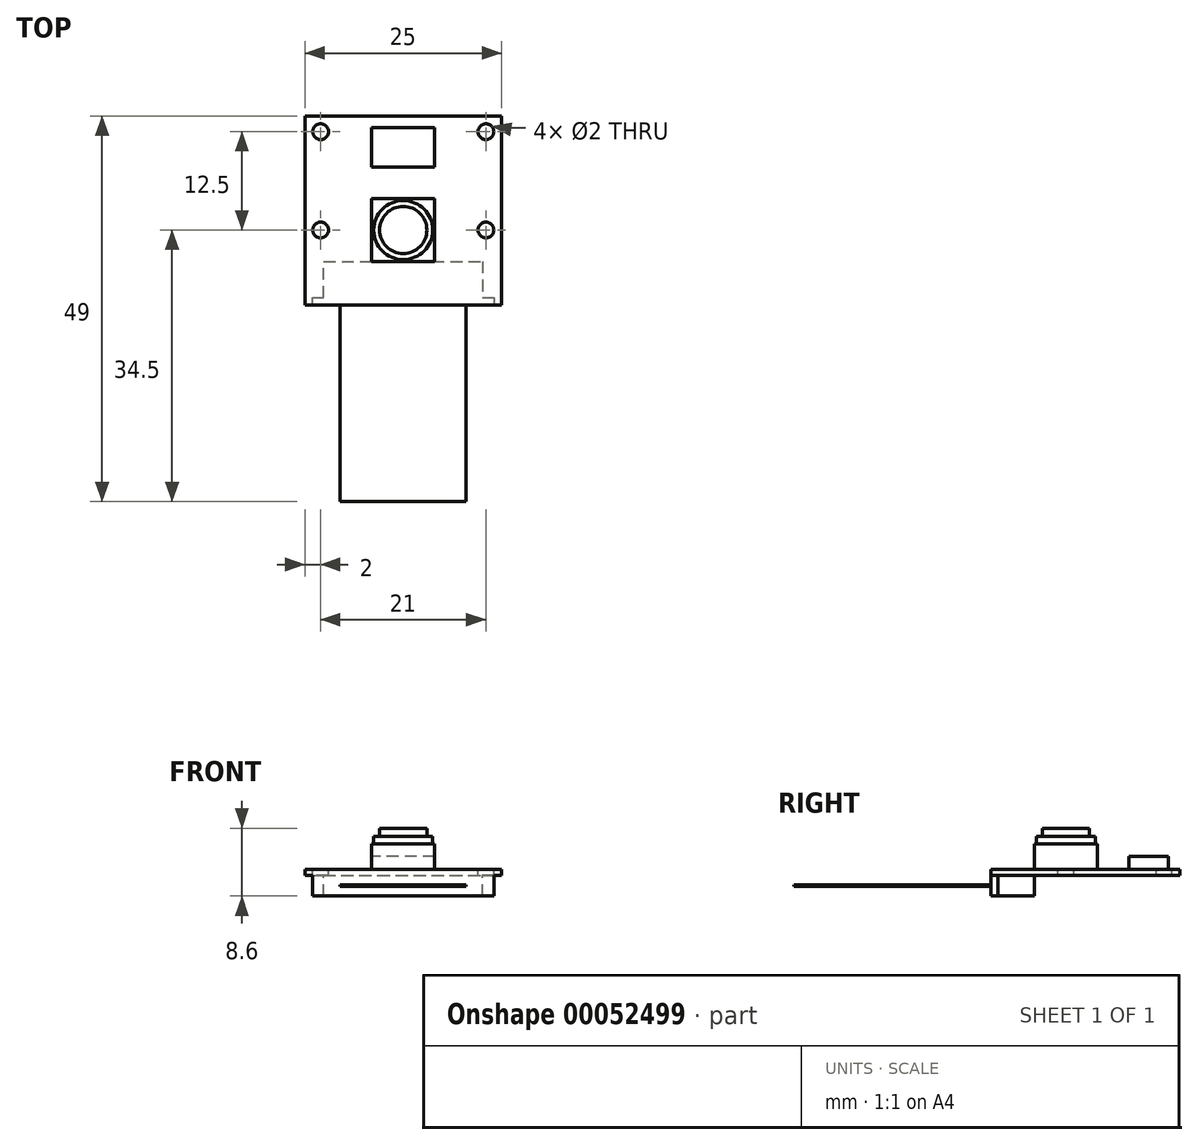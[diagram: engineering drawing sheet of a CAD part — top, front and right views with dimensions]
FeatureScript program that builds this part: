
annotation { "Feature Type Name" : "Feature", "Feature Type Description" : "" }
export const myFeature = defineFeature(function(context is Context, id is Id, definition is map)
    precondition{}
    {
        {
            var Q0;
            Q0=qCreatedBy(makeId("Top.planeOp"),FACE);
            var sketch = newSketch(context, id + "F0", { "sketchPlane" : qUnion([Q0])});
            skLineSegment(sketch, "E0.bottom", {"start": v(-12.5, 14.5) * mm, "end": v(12.5, 14.5) * mm});
            skLineSegment(sketch, "E0.top", {"start": v(-12.5, -9.5) * mm, "end": v(12.5, -9.5) * mm});
            skLineSegment(sketch, "E0.left", {"start": v(-12.5, 14.5) * mm, "end": v(-12.5, -9.5) * mm});
            skLineSegment(sketch, "E0.right", {"start": v(12.5, 14.5) * mm, "end": v(12.5, -9.5) * mm});
            skSolve(sketch);
        }
        {
            var Q0;
            Q0 = qSketchRegion(id + "F0", true);
            extrude(context, id + "F1", {"entities" : qUnion([Q0]), "oppositeDirection" : true, "depth" : .8 * mm});
        }
        {
            var Q0;
            Q0=makeQuery(id+"F1.opExtrude","CAP_FACE",FACE,{"disambiguationData":[OSD([sQuery(id+"F0.wireOp",EDGE,"E0.bottom"),sQuery(id+"F0.wireOp",EDGE,"E0.top"),sQuery(id+"F0.wireOp",EDGE,"E0.left"),sQuery(id+"F0.wireOp",EDGE,"E0.right")])],"isStart":true});
            var sketch = newSketch(context, id + "F2", { "sketchPlane" : qUnion([Q0])});
            skLineSegment(sketch, "E1.rect.bottom", {"start": v(4, 4) * mm, "end": v(-4, 4) * mm});
            skLineSegment(sketch, "E1.rect.top", {"start": v(4, -4) * mm, "end": v(-4, -4) * mm});
            skLineSegment(sketch, "E1.rect.left", {"start": v(4, 4) * mm, "end": v(4, -4) * mm});
            skLineSegment(sketch, "E1.rect.right", {"start": v(-4, 4) * mm, "end": v(-4, -4) * mm});
            skPoint(sketch, "E1.rect.middle", {"position": v(0, 0) * mm});
            skSolve(sketch);
        }
        {
            var Q0;
            Q0 = qSketchRegion(id + "F2", true);
            extrude(context, id + "F3", {"entities" : qUnion([Q0]), "operationType" : NewBodyOperationType.ADD, "depth" : 3.2 * mm});
        }
        {
            var Q0;
            Q0=makeQuery(id+"F3.opExtrude","CAP_FACE",FACE,{"disambiguationData":[OSD([sQuery(id+"F2.wireOp",EDGE,"E1.rect.bottom"),sQuery(id+"F2.wireOp",EDGE,"E1.rect.top"),sQuery(id+"F2.wireOp",EDGE,"E1.rect.left"),sQuery(id+"F2.wireOp",EDGE,"E1.rect.right")])],"isStart":false});
            var sketch = newSketch(context, id + "F4", { "sketchPlane" : qUnion([Q0])});
            skCircle(sketch, "E2", {"center": v(0, 0) * mm, "radius": 3.75 * mm});
            skSolve(sketch);
        }
        {
            var Q0;
            Q0 = qSketchRegion(id + "F4", true);
            var Q1;
            Q1=sQuery(id+"F4.wireOp",EDGE,"E2");
            extrude(context, id + "F5", {"entities" : qUnion([Q0]), "operationType" : NewBodyOperationType.ADD, "surfaceEntities" : qUnion([Q1]), "depth" : 1 * mm});
        }
        {
            var Q0;
            Q0=makeQuery(id+"F5.opExtrude","CAP_FACE",FACE,{"disambiguationData":[OSD([sQuery(id+"F4.wireOp",EDGE,"E2")])],"isStart":false});
            var sketch = newSketch(context, id + "F6", { "sketchPlane" : qUnion([Q0])});
            skCircle(sketch, "E3", {"center": v(0, 0) * mm, "radius": 3 * mm});
            skSolve(sketch);
        }
        {
            var Q0;
            Q0 = qSketchRegion(id + "F6", true);
            extrude(context, id + "F7", {"entities" : qUnion([Q0]), "operationType" : NewBodyOperationType.ADD, "depth" : 1 * mm});
        }
        {
            var Q0;
            Q0=makeQuery(id+"F1.opExtrude","CAP_FACE",FACE,{"disambiguationData":[OSD([sQuery(id+"F0.wireOp",EDGE,"E0.bottom"),sQuery(id+"F0.wireOp",EDGE,"E0.top"),sQuery(id+"F0.wireOp",EDGE,"E0.left"),sQuery(id+"F0.wireOp",EDGE,"E0.right")])],"isStart":true});
            var sketch = newSketch(context, id + "F8", { "sketchPlane" : qUnion([Q0])});
            skPoint(sketch, "E4", {"position": v(-10.5, 12.5) * mm});
            skPoint(sketch, "E5", {"position": v(10.5, 12.5) * mm});
            skPoint(sketch, "E6", {"position": v(10.5, 0) * mm});
            skPoint(sketch, "E7", {"position": v(-10.5, 0) * mm});
            skSolve(sketch);
        }
        {
            var Q0;
            Q0=sQuery(id+"F8.wireOp",VERTEX,"E4");
            var Q1;
            Q1=sQuery(id+"F8.wireOp",VERTEX,"E5");
            var Q2;
            Q2=sQuery(id+"F8.wireOp",VERTEX,"E6");
            var Q3;
            Q3=sQuery(id+"F8.wireOp",VERTEX,"E7");
            var Q4;
            Q4=makeQuery(id+"F1.opExtrude","SWEPT_BODY",BODY,{"disambiguationData":[OSD([sQuery(id+"F0.wireOp",EDGE,"E0.bottom"),sQuery(id+"F0.wireOp",EDGE,"E0.top"),sQuery(id+"F0.wireOp",EDGE,"E0.left"),sQuery(id+"F0.wireOp",EDGE,"E0.right")])]});
            hole(context, id + "F9", {"style" : HoleStyle.SIMPLE, "holeDiameter" : 2 * mm, "endStyle" : HoleEndStyle.THROUGH, "locations" : qUnion([Q0, Q1, Q2, Q3]), "scope" : qUnion([Q4])});
        }
        {
            var Q0;
            Q0=makeQuery(id+"F1.opExtrude","CAP_FACE",FACE,{"disambiguationData":[OSD([sQuery(id+"F0.wireOp",EDGE,"E0.bottom"),sQuery(id+"F0.wireOp",EDGE,"E0.top"),sQuery(id+"F0.wireOp",EDGE,"E0.left"),sQuery(id+"F0.wireOp",EDGE,"E0.right")])],"isStart":true});
            var sketch = newSketch(context, id + "F10", { "sketchPlane" : qUnion([Q0])});
            skLineSegment(sketch, "E8.bottom", {"start": v(4, 8) * mm, "end": v(-4, 8) * mm});
            skLineSegment(sketch, "E8.top", {"start": v(4, 13) * mm, "end": v(-4, 13) * mm});
            skLineSegment(sketch, "E8.left", {"start": v(4, 8) * mm, "end": v(4, 13) * mm});
            skLineSegment(sketch, "E8.right", {"start": v(-4, 8) * mm, "end": v(-4, 13) * mm});
            skSolve(sketch);
        }
        {
            var Q0;
            Q0 = qSketchRegion(id + "F10", true);
            extrude(context, id + "F11", {"entities" : qUnion([Q0]), "operationType" : NewBodyOperationType.ADD, "depth" : 1.6 * mm});
        }
        {
            var Q0;
            Q0=makeQuery(id+"F1.opExtrude","CAP_FACE",FACE,{"disambiguationData":[OSD([sQuery(id+"F0.wireOp",EDGE,"E0.bottom"),sQuery(id+"F0.wireOp",EDGE,"E0.top"),sQuery(id+"F0.wireOp",EDGE,"E0.left"),sQuery(id+"F0.wireOp",EDGE,"E0.right")])],"isStart":false});
            var sketch = newSketch(context, id + "F12", { "sketchPlane" : qUnion([Q0])});
            skLineSegment(sketch, "E9", {"start": v(-11.5, 9.5) * mm, "end": v(-11.5, 8.6) * mm});
            skLineSegment(sketch, "E10", {"start": v(-11.5, 8.6) * mm, "end": v(-10.1, 8.6) * mm});
            skLineSegment(sketch, "E11", {"start": v(-10.1, 8.6) * mm, "end": v(-10.1, 4) * mm});
            skLineSegment(sketch, "E12", {"start": v(-10.1, 4) * mm, "end": v(10.1, 4) * mm});
            skLineSegment(sketch, "E13", {"start": v(10.1, 4) * mm, "end": v(10.1, 8.6) * mm});
            skLineSegment(sketch, "E14", {"start": v(10.1, 8.6) * mm, "end": v(11.5, 8.6) * mm});
            skLineSegment(sketch, "E15", {"start": v(11.5, 8.6) * mm, "end": v(11.5, 9.5) * mm});
            skLineSegment(sketch, "E16", {"start": v(11.5, 9.5) * mm, "end": v(-11.5, 9.5) * mm});
            skSolve(sketch);
        }
        {
            var Q0;
            Q0 = qSketchRegion(id + "F12", true);
            extrude(context, id + "F13", {"entities" : qUnion([Q0]), "operationType" : NewBodyOperationType.ADD, "depth" : 2.6 * mm});
        }
        {
            var Q0;
            Q0=makeQuery(id+"F13.boolean.opBoolean","MERGE",FACE,{"derivedFrom":[makeQuery(id+"F1.opExtrude","SWEPT_FACE",FACE,{"disambiguationData":[OSD([sQuery(id+"F0.wireOp",EDGE,"E0.top")])]}),makeQuery(id+"F13.opExtrude","SWEPT_FACE",FACE,{"disambiguationData":[OSD([sQuery(id+"F12.wireOp",EDGE,"E16")])]})]});
            var sketch = newSketch(context, id + "F14", { "sketchPlane" : qUnion([Q0])});
            skLineSegment(sketch, "E17.bottom", {"start": v(-8, -2) * mm, "end": v(8, -2) * mm});
            skLineSegment(sketch, "E17.top", {"start": v(-8, -2.15) * mm, "end": v(8, -2.15) * mm});
            skLineSegment(sketch, "E17.left", {"start": v(-8, -2) * mm, "end": v(-8, -2.15) * mm});
            skLineSegment(sketch, "E17.right", {"start": v(8, -2) * mm, "end": v(8, -2.15) * mm});
            skSolve(sketch);
        }
        {
            var Q0;
            Q0 = qSketchRegion(id + "F14", true);
            extrude(context, id + "F15", {"entities" : qUnion([Q0]), "operationType" : NewBodyOperationType.ADD, "depth" : 25 * mm});
        }
    });
